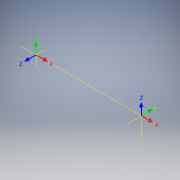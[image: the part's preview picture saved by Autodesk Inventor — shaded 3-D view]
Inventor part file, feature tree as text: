
AUTODESK INVENTOR PART (.ipt)
format: ipt  version: 2019 (Build 230136000, 136)  size: 108,032 bytes
history: native  units: in
note: dims shown in document units (in); Inventor stores cm internally (conversion verified against a paired STEP export)
features: other x19, sketch x2, plane x1
ambient origin geometry x4: Origin, YZ Plane, XZ Plane, XY Plane
feature tree (22):
  parser-record x1  (decoder bookkeeping rows leaked as tree rows — omitted from the tree; the rows remain in map.json)
  other  "d offset"
  other  "theta offset"
  other  "r_offset"
  other  "alpha offset"
  sketch  "Sketch4"  dims[d0=0.0in d1=0.0in d2=0.0in d3=0.0in d4=0.0in d5=0.0in d7=4.4094in d8=0.0in d11=0.0in d12=0.0in d13=0.0394in d14=0.0394in d15=0.0in d16=0.0in d17=0.0in d18=0.0in d19=0.0in d20=0.0in]
  sketch  "3D Sketch2"
  plane  "Work Plane5"
  other  "UCS5: YZ Plane"
  other  "UCS5: XZ Plane"
  other  "UCS5: XY Plane"
  other  "UCS5: X Axis"
  other  "UCS5: Y Axis"
  other  "UCS5: Z Axis"
  other  "UCS5: Center Point"
  other  "UCS6: YZ Plane"
  other  "UCS6: XZ Plane"
  other  "UCS6: XY Plane"
  other  "UCS6: X Axis"
  other  "UCS6: Y Axis"
  other  "UCS6: Z Axis"
  other  "UCS6: Center Point"
note: 1 file-system path scrubbed to <path> (originals preserved in map.json)
